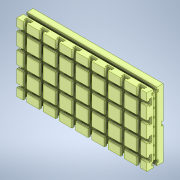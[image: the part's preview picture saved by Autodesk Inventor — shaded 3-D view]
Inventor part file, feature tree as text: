
AUTODESK INVENTOR PART (.ipt)
format: ipt  version: 2021 (Build 250183000, 183)  size: 1,294,848 bytes
history: native  units: mm
features: sketch x9, other x5, pattern_linear x5, mirror x3, hole x3, extrude x1
ambient origin geometry x8: Origin, YZ Plane, XZ Plane, XY Plane, X Axis, Y Axis, Z Axis, Center Point
bodies: Solid1 (feature_tree)
feature tree (26):
  extrude  "Extrusion1"  Depth=268.0mm
  other  "iFeature2:1"
  other  "iFeature2:2"
  pattern_linear  "Rectangular Pattern1"  Spacing1=7.0mm  [1 undecoded]
  pattern_linear  "Rectangular Pattern2"  Spacing1=38.0mm  [1 undecoded]
  other  "iFeature2:3"
  mirror  "Mirror1"
  other  "iFeature4:1"
  other  "iFeature4:2"
  mirror  "Mirror2"
  hole  "Hole1"  [1 undecoded]
  pattern_linear  "Rectangular Pattern3"  Spacing1=64.0mm  [1 undecoded]
  mirror  "Mirror3"
  hole  "Hole2"  [1 undecoded]
  pattern_linear  "Rectangular Pattern4"  Spacing1=64.0mm  [1 undecoded]
  hole  "Hole3"  [1 undecoded]
  pattern_linear  "Rectangular Pattern5"  Spacing1=32.0mm  [1 undecoded]
  sketch  "Sketch1"  dims[d0=512.0mm d1=268.0mm]
  sketch  "Sketch7"  dims[d11=7.0mm]
  sketch  "Sketch8"  dims[d12=32.0mm]
  sketch  "Sketch9"  dims[d13=10.0mm d14=9.0mm d15=14.0mm d16=25.0mm d17=12.5mm d18=7.0mm d19=38.0mm d20=80.0mm d22=64.0mm d23=40.0mm d25=64.0mm d26=10.0mm d27=9.0mm d28=14.0mm d29=25.0mm d30=12.5mm d31=7.0mm d32=32.0mm d33=7.0mm d34=2.0mm d35=2.0mm d36=90.0deg d37=2.0mm d38=135.0deg d39=5.0mm d40=7.0mm d41=2.0mm d42=2.0mm d43=90.0deg d44=2.0mm d45=135.0deg d46=5.0mm d47=32.0mm d48=38.0mm d49=32.0mm d50=4.917mm d51=10.0mm d52=4.0mm d53=2.0mm d54=90.0deg d55=15.0mm d56=20.594885mm d57=70.0mm d59=32.0mm d60=64.0mm d61=70.0mm d62=46.0mm d63=10.0mm d64=4.0mm d65=2.0mm d66=90.0deg d67=35.0mm d68=20.594885mm d69=70.0mm d71=64.0mm d72=30.0mm d74=64.0mm d75=32.0mm d76=134.0mm d77=4.917mm d78=10.0mm d79=4.0mm d80=2.0mm d81=90.0deg d82=15.0mm d83=20.594885mm d84=90.0mm d86=64.0mm d58=0.75mm]
  sketch  "Sketch2"  dims[d2=256.0mm]
  sketch  "Sketch3"  dims[d3=134.0mm]
  sketch  "Sketch4"  dims[d4=64.0mm]
  sketch  "Sketch5"  dims[d5=0.0mm]
  sketch  "Sketch6"  dims[d6=10.0mm d7=9.0mm d8=14.0mm d9=25.0mm d10=12.5mm]
note: 8 required parameter values undecoded (feature->parameter linkage not recoverable at this tier; creation-order binding heuristic only, values carry confidence <= 0.55)
